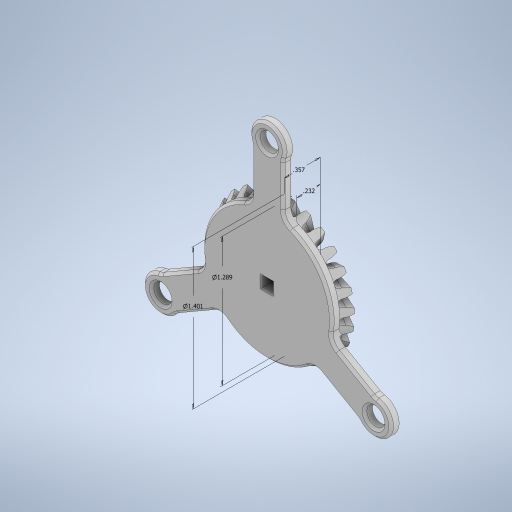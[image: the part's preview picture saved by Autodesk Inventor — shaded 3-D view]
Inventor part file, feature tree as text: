
AUTODESK INVENTOR PART (.ipt)
format: ipt  version: 2023 (Build 270158000, 158)  size: 1,174,016 bytes
history: native  units: in
note: dims shown in document units (in); Inventor stores cm internally (conversion verified against a paired STEP export)
features: sketch x4, extrude x3, move_body x2, other x2, pattern_circular x2, revolve x1, loft x1, boolean_combine x1, fillet x1, chamfer x1
ambient origin geometry x8: Origin, YZ Plane, XZ Plane, XY Plane, X Axis, Y Axis, Z Axis, Center Point
bodies: Solid3 (feature_tree), Solid4 (feature_tree), Solid5 (feature_tree)
feature tree (18):
  sketch  "Sketch1"  dims[d3=1.289in d4=1.401in]
  revolve  "Revolution1"  [1 undecoded]
  extrude  "Extrusion2"  Depth=0.232in
  move_body  "Move Body1"
  move_body  "Move Body2"
  other  "Work Point1"
  loft  "Loft1"
  boolean_combine  "Combine1"
  pattern_circular  "Circular Pattern1"  [2 undecoded]
  extrude  "Extrusion3"  TaperAngle=0.0deg  [1 undecoded]
  fillet  "Fillet1"  [1 undecoded]
  pattern_circular  "Circular Pattern2"  Count=27 Angle=360.0deg
  extrude  "Extrusion4"  Depth=0.18in
  chamfer  "Chamfer2"  Distance=0.3125in
  sketch  "Sketch2"  dims[d5=0.357in d6=0.232in]
  other  "Edges1"
  sketch  "Sketch3"  dims[d7=90.0deg d8=0.0039in d9=0.0in]
  sketch  "Sketch4"  dims[d10=0.4078in d11=0.0in d12=-0.019in d13=-0.102in d14=0.0in d15=90.0deg d16=0.0in d17=90.0deg d18=10.6299in d19=360.0deg d21=0.18in d23=0.3125in d25=2.45in d26=0.35in d27=1.1811in d29=360.0deg d31=0.0787in d32=0.0in d33=0.125in d34=1.1811in d35=360.0deg d40=0.13in d41=0.13in d42=0.0in d43=0.0in d44=0.0236in d45=0.125in d46=45.0deg]
note: 5 required parameter values undecoded (feature->parameter linkage not recoverable at this tier; creation-order binding heuristic only, values carry confidence <= 0.55)